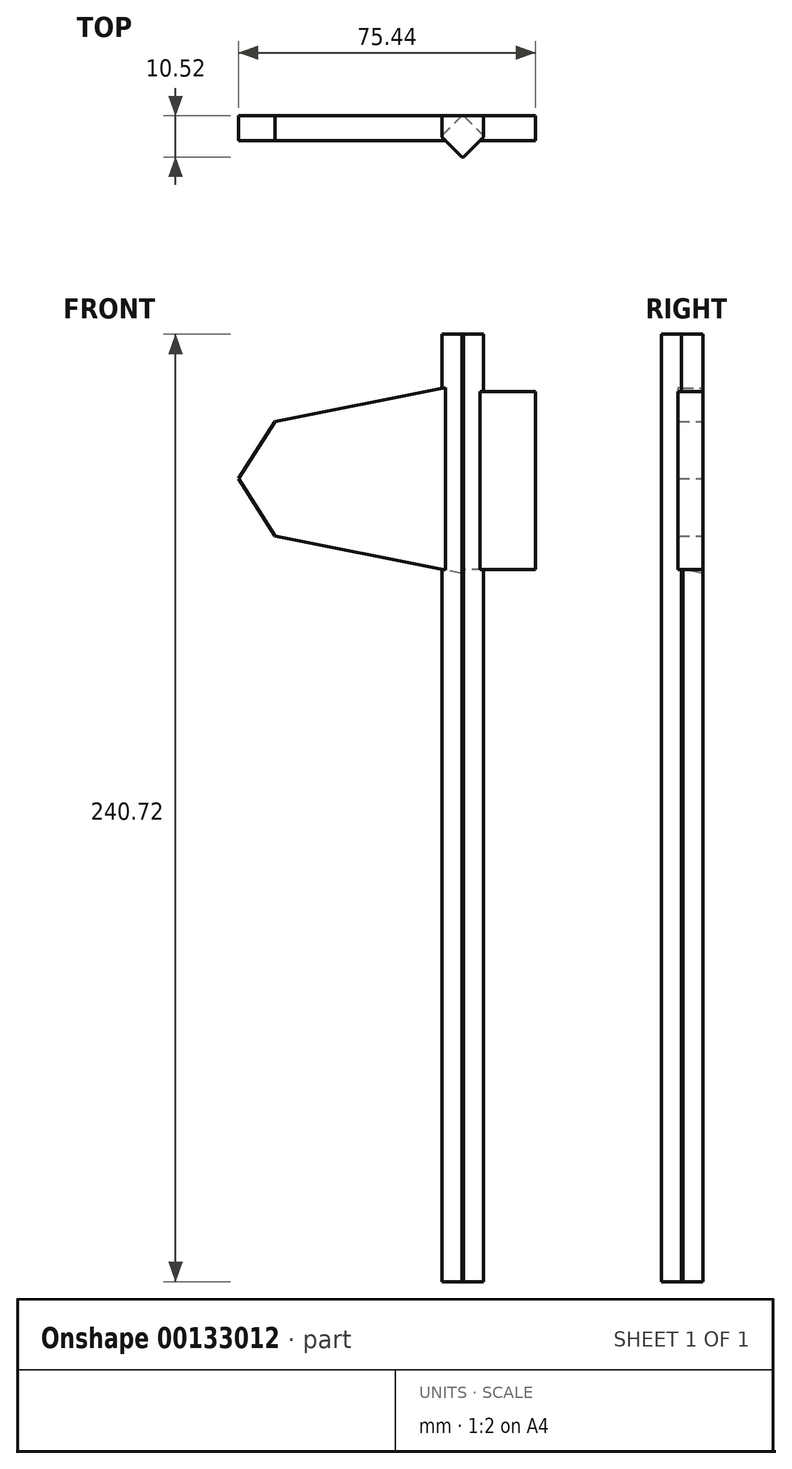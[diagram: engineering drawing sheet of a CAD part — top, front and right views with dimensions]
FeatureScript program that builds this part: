
annotation { "Feature Type Name" : "Feature", "Feature Type Description" : "" }
export const myFeature = defineFeature(function(context is Context, id is Id, definition is map)
    precondition{}
    {
        {
            var Q0;
            Q0=qCreatedBy(makeId("Front.planeOp"),FACE);
            var sketch = newSketch(context, id + "F0", { "sketchPlane" : qUnion([Q0])});
            skLineSegment(sketch, "E0", {"start": v(42.24, 30.32) * mm, "end": v(42.24, -210.4) * mm});
            skLineSegment(sketch, "E1", {"start": v(42.24, -210.4) * mm, "end": v(31.63, -210.4) * mm});
            skLineSegment(sketch, "E2", {"start": v(31.63, -210.4) * mm, "end": v(31.63, 30.32) * mm});
            skLineSegment(sketch, "E3", {"start": v(31.63, 30.32) * mm, "end": v(42.24, 30.32) * mm});
            skLineSegment(sketch, "E4", {"start": v(42.24, 15.8) * mm, "end": v(55.43, 15.8) * mm});
            skLineSegment(sketch, "E5", {"start": v(55.43, 15.8) * mm, "end": v(55.43, -29.38) * mm});
            skLineSegment(sketch, "E6", {"start": v(55.43, -29.38) * mm, "end": v(42.24, -29.38) * mm});
            skPoint(sketch, "E7.endSnap0", {"position": v(55.43, -6.8) * mm});
            skLineSegment(sketch, "E8", {"start": v(31.63, -29.38) * mm, "end": v(-10.73, -20.91) * mm});
            skLineSegment(sketch, "E9", {"start": v(-10.73, -20.91) * mm, "end": v(-20, -6.4) * mm});
            skLineSegment(sketch, "E10.MirrorCS", {"start": v(-10.73, 8.13) * mm, "end": v(-20, -6.4) * mm});
            skLineSegment(sketch, "E11.MirrorCS", {"start": v(31.63, 16.6) * mm, "end": v(-10.73, 8.13) * mm});
            skLineSegment(sketch, "E12", {"start": v(31.63, -29.38) * mm, "end": v(42.24, -29.38) * mm});
            skLineSegment(sketch, "E13", {"start": v(31.63, 16.6) * mm, "end": v(42.24, 15.8) * mm});
            skSolve(sketch);
        }
        {
            var Q0;
            {var subQ0=sQuery(id+"F0.wireOp",EDGE,"E1");Q0=makeQuery(id+"F0.imprint","IMPRINT",FACE,{"disambiguationData":[TD([[makeQuery(id+"F0.imprint","IMPRINT",EDGE,{"derivedFrom":subQ0}),-1.0]])]});}
            var Q1;
            {var subQ0=sQuery(id+"F0.wireOp",EDGE,"E3");Q1=makeQuery(id+"F0.imprint","IMPRINT",FACE,{"disambiguationData":[TD([[makeQuery(id+"F0.imprint","IMPRINT",EDGE,{"derivedFrom":subQ0}),-1.0]])]});}
            var Q2;
            {var subQ2=sQuery(id+"F0.wireOp",EDGE,"E12");Q2=makeQuery(id+"F0.imprint","IMPRINT",FACE,{"disambiguationData":[TD([[makeQuery(id+"F0.imprint","IMPRINT",EDGE,{"derivedFrom":subQ2}),1.0]])]});}
            extrude(context, id + "F1", {"entities" : qUnion([Q0, Q1, Q2]), "depth" : 10.52 * mm});
        }
        {
            var Q0;
            Q0 = qSketchRegion(id + "F0", true);
            extrude(context, id + "F2", {"entities" : qUnion([Q0]), "operationType" : NewBodyOperationType.ADD, "depth" : 6.38 * mm});
        }
        {
            var Q0;
            Q0=makeQuery(id+"F1.opExtrude","CAP_EDGE",EDGE,{"disambiguationData":[OSD([sQuery(id+"F0.wireOp",EDGE,"E0")])],"isStart":false});
            var Q1;
            Q1=makeQuery(id+"F1.opExtrude","CAP_EDGE",EDGE,{"disambiguationData":[OSD([sQuery(id+"F0.wireOp",EDGE,"E2")])],"isStart":false});
            var Q2;
            {var subQ3=sQuery(id+"F0.wireOp",EDGE,"E1");var subQ4=sQuery(id+"F0.wireOp",EDGE,"E0");Q2=makeQuery(id+"F2.boolean.opBoolean","SPLIT",EDGE,{"disambiguationData":[TD([makeQuery(id+"F1.opExtrude","SWEPT_FACE",FACE,{"disambiguationData":[OSD([subQ3])]})])],"derivedFrom":makeQuery(id+"F1.opExtrude","CAP_EDGE",EDGE,{"disambiguationData":[OSD([subQ4])],"isStart":true})});}
            var Q3;
            {var subQ2=sQuery(id+"F0.wireOp",EDGE,"E2");var subQ3=sQuery(id+"F0.wireOp",EDGE,"E1");Q3=makeQuery(id+"F2.boolean.opBoolean","SPLIT",EDGE,{"disambiguationData":[TD([makeQuery(id+"F1.opExtrude","SWEPT_FACE",FACE,{"disambiguationData":[OSD([subQ3])]})])],"derivedFrom":makeQuery(id+"F1.opExtrude","CAP_EDGE",EDGE,{"disambiguationData":[OSD([subQ2])],"isStart":true})});}
            chamfer(context, id + "F3", {"entities" : qUnion([Q0, Q1, Q2, Q3]), "width" : 5.08 * mm, "tangentPropagation" : true});
        }
    });
